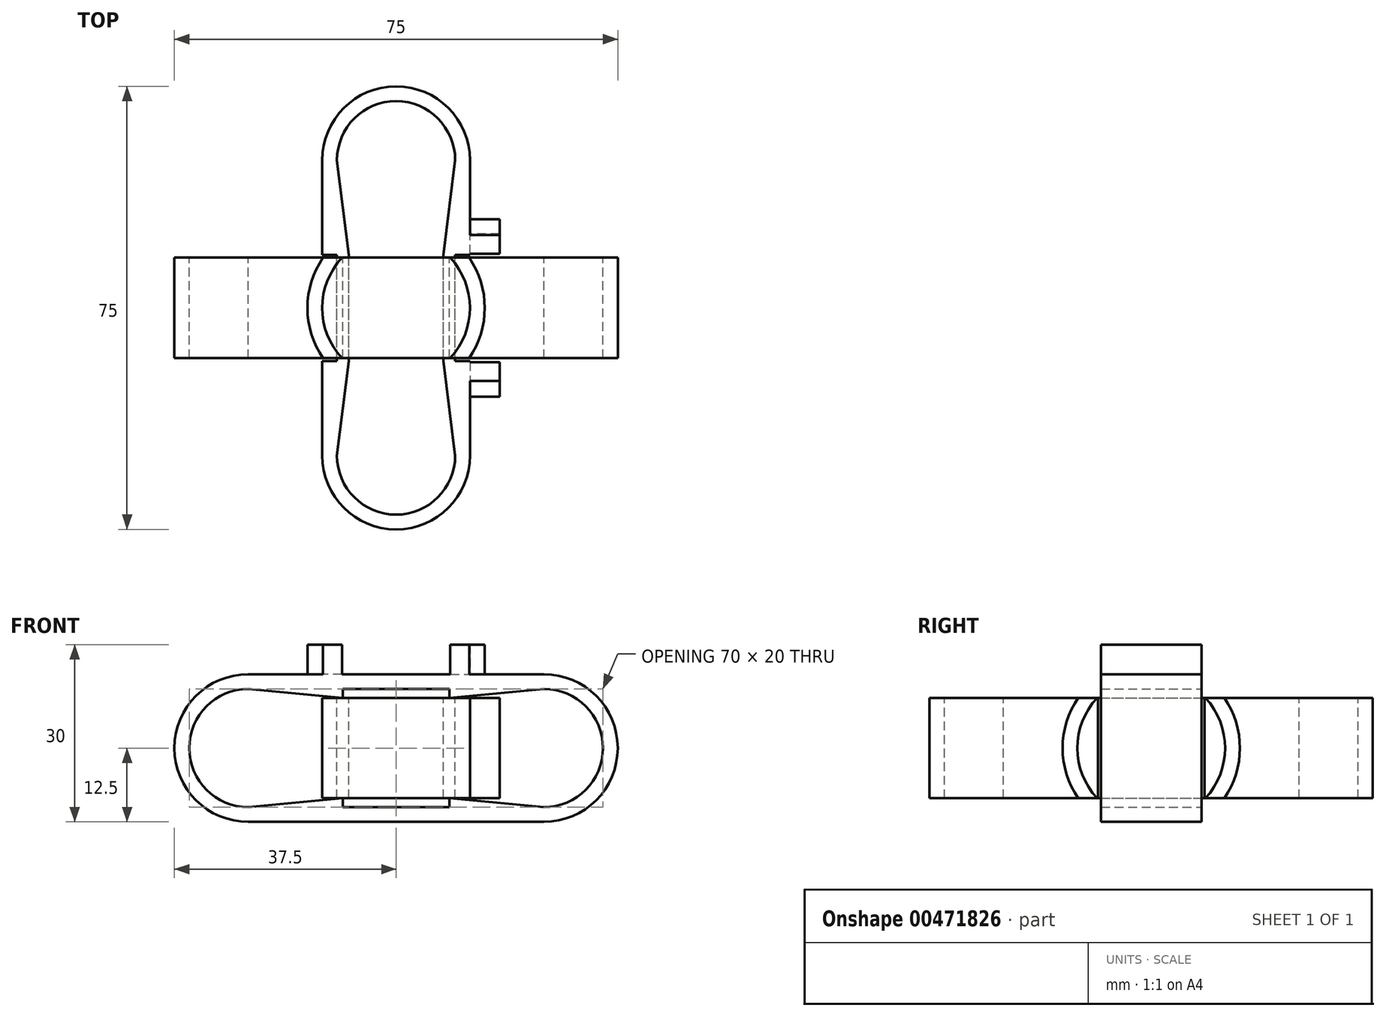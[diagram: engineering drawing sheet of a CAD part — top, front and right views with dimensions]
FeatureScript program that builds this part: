
annotation { "Feature Type Name" : "Feature", "Feature Type Description" : "" }
export const myFeature = defineFeature(function(context is Context, id is Id, definition is map)
    precondition{}
    {
        {
            var Q0;
            Q0=qCreatedBy(makeId("Front.planeOp"),FACE);
            var sketch = newSketch(context, id + "F0", { "sketchPlane" : qUnion([Q0])});
            skArc(sketch, "E0", {"start": v(-25, 12.5) * mm, "mid": v(-37.5, 0) * mm, "end": v(-25, -12.5) * mm});
            skArc(sketch, "E1", {"start": v(25, -12.5) * mm, "mid": v(37.5, 0) * mm, "end": v(25, 12.5) * mm});
            skLineSegment(sketch, "E2", {"start": v(-25, 12.5) * mm, "end": v(25, 12.5) * mm});
            skLineSegment(sketch, "E3", {"start": v(-25, -12.5) * mm, "end": v(25, -12.5) * mm});
            skPoint(sketch, "E4", {"position": v(0, 12.5) * mm});
            skArc(sketch, "E5.0", {"start": v(-25, 10) * mm, "mid": v(-35, 0) * mm, "end": v(-25, -10) * mm});
            skLineSegment(sketch, "E5.1", {"start": v(-9, 10) * mm, "end": v(9, 10) * mm});
            skArc(sketch, "E5.2", {"start": v(25, -10) * mm, "mid": v(35, 0) * mm, "end": v(25, 10) * mm});
            skLineSegment(sketch, "E5.3", {"start": v(-9, -10) * mm, "end": v(9, -10) * mm});
            skLineSegment(sketch, "E6", {"start": v(-9, 10) * mm, "end": v(-9, 8.5) * mm});
            skLineSegment(sketch, "E7", {"start": v(9, 8.5) * mm, "end": v(9, 10) * mm});
            skLineSegment(sketch, "E8", {"start": v(-25, 10) * mm, "end": v(-9, 8.5) * mm});
            skLineSegment(sketch, "E9", {"start": v(9, 8.5) * mm, "end": v(25, 10) * mm});
            skLineSegment(sketch, "E10", {"start": v(-25, 0) * mm, "end": v(25, 0) * mm, "construction": true});
            skPoint(sketch, "E11", {"position": v(0, 10) * mm});
            skLineSegment(sketch, "E12.MirrorCS", {"start": v(-25, -10) * mm, "end": v(-9, -8.5) * mm});
            skLineSegment(sketch, "E13.MirrorCS", {"start": v(-9, -10) * mm, "end": v(-9, -8.5) * mm});
            skLineSegment(sketch, "E14.MirrorCS", {"start": v(9, -8.5) * mm, "end": v(9, -10) * mm});
            skLineSegment(sketch, "E15.MirrorCS", {"start": v(9, -8.5) * mm, "end": v(25, -10) * mm});
            skSolve(sketch);
        }
        {
            var Q0;
            Q0=makeQuery(id+"F0.imprint","IMPRINT",FACE,{"disambiguationData":[TD([[makeQuery(id+"F0.imprint","IMPRINT",EDGE,{"derivedFrom":sQuery(id+"F0.wireOp",EDGE,"E0")}),1.0]])]});
            extrude(context, id + "F1", {"entities" : qUnion([Q0]), "depth" : 8.5 * mm, "hasSecondDirection" : true, "secondDirectionOppositeDirection" : true, "secondDirectionDepth" : 8.5 * mm});
        }
        {
            var Q0;
            Q0=qCreatedBy(makeId("Right.planeOp"),FACE);
            var sketch = newSketch(context, id + "F2", { "sketchPlane" : qUnion([Q0])});
            skArc(sketch, "E16", {"start": v(-25, 12.5) * mm, "mid": v(-37.5, 0) * mm, "end": v(-25, -12.5) * mm});
            skArc(sketch, "E17", {"start": v(25, -12.5) * mm, "mid": v(37.5, 0) * mm, "end": v(25, 12.5) * mm});
            skLineSegment(sketch, "E18", {"start": v(-25, 12.5) * mm, "end": v(-9, 12.5) * mm});
            skArc(sketch, "E19.0", {"start": v(-25, 10) * mm, "mid": v(-35, 0) * mm, "end": v(-25, -10) * mm});
            skLineSegment(sketch, "E19.1", {"start": v(-9, 10) * mm, "end": v(9, 10) * mm});
            skArc(sketch, "E19.2", {"start": v(25, -10) * mm, "mid": v(35, 0) * mm, "end": v(25, 10) * mm});
            skLineSegment(sketch, "E20", {"start": v(-25, 10) * mm, "end": v(-9, 8) * mm});
            skLineSegment(sketch, "E21", {"start": v(9, 8) * mm, "end": v(25, 10) * mm});
            skLineSegment(sketch, "E22", {"start": v(-25, 0) * mm, "end": v(25, 0) * mm, "construction": true});
            skPoint(sketch, "E23", {"position": v(0, 10) * mm});
            skLineSegment(sketch, "E24", {"start": v(-9, 12.5) * mm, "end": v(-9, 10) * mm});
            skLineSegment(sketch, "E25", {"start": v(9, 12.5) * mm, "end": v(9, 10) * mm});
            skLineSegment(sketch, "E26.trimOffspring", {"start": v(9, 12.5) * mm, "end": v(25, 12.5) * mm});
            skLineSegment(sketch, "E27", {"start": v(-9, 8) * mm, "end": v(9, 8) * mm});
            skPoint(sketch, "E28", {"position": v(0, 8) * mm});
            skLineSegment(sketch, "E29.MirrorCS", {"start": v(-25, -10) * mm, "end": v(-9, -8) * mm});
            skLineSegment(sketch, "E30.MirrorCS", {"start": v(-25, -12.5) * mm, "end": v(-9, -12.5) * mm});
            skLineSegment(sketch, "E31.MirrorCS", {"start": v(-9, -12.5) * mm, "end": v(-9, -10) * mm});
            skLineSegment(sketch, "E32.MirrorCS", {"start": v(-9, -10) * mm, "end": v(9, -10) * mm});
            skLineSegment(sketch, "E33.MirrorCS", {"start": v(-9, -8) * mm, "end": v(9, -8) * mm});
            skLineSegment(sketch, "E34.MirrorCS", {"start": v(9, -8) * mm, "end": v(25, -10) * mm});
            skLineSegment(sketch, "E35.MirrorCS", {"start": v(9, -12.5) * mm, "end": v(9, -10) * mm});
            skLineSegment(sketch, "E36.MirrorCS", {"start": v(9, -12.5) * mm, "end": v(25, -12.5) * mm});
            skSolve(sketch);
        }
        {
            var Q0;
            Q0=makeQuery(id+"F2.imprint","IMPRINT",FACE,{"disambiguationData":[TD([[makeQuery(id+"F2.imprint","IMPRINT",EDGE,{"derivedFrom":sQuery(id+"F2.wireOp",EDGE,"E16")}),1.0]])]});
            extrude(context, id + "F3", {"entities" : qUnion([Q0]), "depth" : 8.5 * mm, "hasSecondDirection" : true, "secondDirectionOppositeDirection" : true, "secondDirectionDepth" : 8.5 * mm});
        }
        {
            var Q0;
            Q0=makeQuery(id+"F1.opExtrude","SWEPT_FACE",FACE,{"disambiguationData":[OSD([sQuery(id+"F0.wireOp",EDGE,"E2")])]});
            var sketch = newSketch(context, id + "F4", { "sketchPlane" : qUnion([Q0])});
            skCircle(sketch, "E37", {"center": v(0, 0) * mm, "radius": 12.5 * mm});
            skCircle(sketch, "E38.0", {"center": v(0, 0) * mm, "radius": 15 * mm});
            skLineSegment(sketch, "E39", {"start": v(-8.67, 9) * mm, "end": v(-10.4, 10.8) * mm});
            skLineSegment(sketch, "E40", {"start": v(8.67, 9) * mm, "end": v(10.4, 10.8) * mm});
            skLineSegment(sketch, "E41", {"start": v(-8.67, 9) * mm, "end": v(0, 0) * mm, "construction": true});
            skLineSegment(sketch, "E42", {"start": v(0, 0) * mm, "end": v(8.67, 9) * mm, "construction": true});
            skLineSegment(sketch, "E43", {"start": v(0, 0) * mm, "end": v(-12.36, 8.5) * mm});
            skLineSegment(sketch, "E44", {"start": v(0, 0) * mm, "end": v(12.36, 8.5) * mm});
            skLineSegment(sketch, "E45", {"start": v(-12.5, 0) * mm, "end": v(12.5, 0) * mm, "construction": true});
            skLineSegment(sketch, "E46.MirrorCS", {"start": v(0, 0) * mm, "end": v(-12.36, -8.5) * mm});
            skLineSegment(sketch, "E47.MirrorCS", {"start": v(-8.67, -9) * mm, "end": v(-10.4, -10.8) * mm});
            skLineSegment(sketch, "E48.MirrorCS", {"start": v(8.67, -9) * mm, "end": v(10.4, -10.8) * mm});
            skLineSegment(sketch, "E49.MirrorCS", {"start": v(0, 0) * mm, "end": v(12.36, -8.5) * mm});
            skLineSegment(sketch, "E50.0", {"start": v(-8.5, 9) * mm, "end": v(-8.5, 25) * mm});
            skLineSegment(sketch, "E51.0", {"start": v(8.5, 9) * mm, "end": v(-8.5, 9) * mm});
            skLineSegment(sketch, "E52.0", {"start": v(8.5, 9) * mm, "end": v(8.5, 25) * mm});
            skLineSegment(sketch, "E53.0", {"start": v(8.5, -9) * mm, "end": v(-8.5, -9) * mm});
            skLineSegment(sketch, "E54.0", {"start": v(8.5, -25) * mm, "end": v(8.5, -9) * mm});
            skLineSegment(sketch, "E55.0", {"start": v(-8.5, -25) * mm, "end": v(-8.5, -9) * mm});
            skSolve(sketch);
        }
        {
            var Q0;
            {var subQ0=sQuery(id+"F4.wireOp",EDGE,"E43");var subQ1=sQuery(id+"F4.wireOp",EDGE,"E37");var subQ2=makeQuery(id+"F4.imprint","INTERSECT",VERTEX,{"derivedFrom":[subQ1,subQ0]});Q0=makeQuery(id+"F4.imprint","IMPRINT",FACE,{"disambiguationData":[TD([[makeQuery(id+"F4.imprint","IMPRINT",EDGE,{"disambiguationData":[TD([[subQ2,-1.0]])],"derivedFrom":subQ1}),-1.0]])]});}
            var Q1;
            {var subQ0=sQuery(id+"F4.wireOp",EDGE,"E44");var subQ1=sQuery(id+"F4.wireOp",EDGE,"E37");var subQ2=makeQuery(id+"F4.imprint","INTERSECT",VERTEX,{"derivedFrom":[subQ1,subQ0]});Q1=makeQuery(id+"F4.imprint","IMPRINT",FACE,{"disambiguationData":[TD([[makeQuery(id+"F4.imprint","IMPRINT",EDGE,{"disambiguationData":[TD([[subQ2,1.0]])],"derivedFrom":subQ1}),-1.0]])]});}
            var Q2;
            {var subQ0=sQuery(id+"F4.wireOp",EDGE,"E43");var subQ1=sQuery(id+"F4.wireOp",EDGE,"E37");var subQ2=makeQuery(id+"F4.imprint","INTERSECT",VERTEX,{"derivedFrom":[subQ1,subQ0]});Q2=makeQuery(id+"F4.imprint","IMPRINT",FACE,{"disambiguationData":[TD([[makeQuery(id+"F4.imprint","IMPRINT",EDGE,{"disambiguationData":[TD([[subQ2,1.0]])],"derivedFrom":subQ1}),-1.0]])]});}
            var Q3;
            {var subQ0=sQuery(id+"F4.wireOp",EDGE,"E44");var subQ1=sQuery(id+"F4.wireOp",EDGE,"E37");var subQ2=makeQuery(id+"F4.imprint","INTERSECT",VERTEX,{"derivedFrom":[subQ1,subQ0]});Q3=makeQuery(id+"F4.imprint","IMPRINT",FACE,{"disambiguationData":[TD([[makeQuery(id+"F4.imprint","IMPRINT",EDGE,{"disambiguationData":[TD([[subQ2,-1.0]])],"derivedFrom":subQ1}),-1.0]])]});}
            var Q4;
            {var subQ0=sQuery(id+"F4.wireOp",EDGE,"E49.MirrorCS");var subQ1=sQuery(id+"F4.wireOp",EDGE,"E37");var subQ2=makeQuery(id+"F4.imprint","INTERSECT",VERTEX,{"derivedFrom":[subQ1,subQ0]});Q4=makeQuery(id+"F4.imprint","IMPRINT",FACE,{"disambiguationData":[TD([[makeQuery(id+"F4.imprint","IMPRINT",EDGE,{"disambiguationData":[TD([[subQ2,1.0]])],"derivedFrom":subQ1}),-1.0]])]});}
            var Q5;
            {var subQ0=sQuery(id+"F4.wireOp",EDGE,"E46.MirrorCS");var subQ1=sQuery(id+"F4.wireOp",EDGE,"E37");var subQ2=makeQuery(id+"F4.imprint","INTERSECT",VERTEX,{"derivedFrom":[subQ1,subQ0]});Q5=makeQuery(id+"F4.imprint","IMPRINT",FACE,{"disambiguationData":[TD([[makeQuery(id+"F4.imprint","IMPRINT",EDGE,{"disambiguationData":[TD([[subQ2,-1.0]])],"derivedFrom":subQ1}),-1.0]])]});}
            extrude(context, id + "F5", {"entities" : qUnion([Q0, Q1, Q2, Q3, Q4, Q5]), "operationType" : NewBodyOperationType.ADD, "depth" : 5 * mm});
        }
        {
            var Q0;
            {var subQ0=sQuery(id+"F4.wireOp",EDGE,"E52.0");var subQ1=sQuery(id+"F4.wireOp",EDGE,"E37");var subQ2=makeQuery(id+"F4.imprint","INTERSECT",VERTEX,{"derivedFrom":[subQ1,subQ0]});Q0=makeQuery(id+"F4.imprint","IMPRINT",FACE,{"disambiguationData":[TD([[makeQuery(id+"F4.imprint","IMPRINT",EDGE,{"disambiguationData":[TD([[subQ2,-1.0]])],"derivedFrom":subQ1}),-1.0]])]});}
            var Q1;
            {var subQ0=sQuery(id+"F4.wireOp",EDGE,"E55.0");var subQ1=sQuery(id+"F4.wireOp",EDGE,"E37");var subQ2=makeQuery(id+"F4.imprint","INTERSECT",VERTEX,{"derivedFrom":[subQ1,subQ0]});Q1=makeQuery(id+"F4.imprint","IMPRINT",FACE,{"disambiguationData":[TD([[makeQuery(id+"F4.imprint","IMPRINT",EDGE,{"disambiguationData":[TD([[subQ2,-1.0]])],"derivedFrom":subQ1}),-1.0]])]});}
            extrude(context, id + "F6", {"entities" : qUnion([Q0, Q1]), "operationType" : NewBodyOperationType.ADD, "depth" : 5 * mm});
        }
        {
            var Q0;
            Q0=makeQuery(id+"F3.opExtrude","SWEPT_BODY",BODY,{"disambiguationData":[OSD([sQuery(id+"F2.wireOp",EDGE,"E16"),sQuery(id+"F2.wireOp",EDGE,"E17"),sQuery(id+"F2.wireOp",EDGE,"E18"),sQuery(id+"F2.wireOp",EDGE,"E19.0"),sQuery(id+"F2.wireOp",EDGE,"E19.1"),sQuery(id+"F2.wireOp",EDGE,"E19.2"),sQuery(id+"F2.wireOp",EDGE,"E20"),sQuery(id+"F2.wireOp",EDGE,"E21"),sQuery(id+"F2.wireOp",EDGE,"E24"),sQuery(id+"F2.wireOp",EDGE,"E25"),sQuery(id+"F2.wireOp",EDGE,"E26.trimOffspring"),sQuery(id+"F2.wireOp",EDGE,"E27"),sQuery(id+"F2.wireOp",EDGE,"E29.MirrorCS"),sQuery(id+"F2.wireOp",EDGE,"E30.MirrorCS"),sQuery(id+"F2.wireOp",EDGE,"E31.MirrorCS"),sQuery(id+"F2.wireOp",EDGE,"E32.MirrorCS"),sQuery(id+"F2.wireOp",EDGE,"E33.MirrorCS"),sQuery(id+"F2.wireOp",EDGE,"E34.MirrorCS"),sQuery(id+"F2.wireOp",EDGE,"E35.MirrorCS"),sQuery(id+"F2.wireOp",EDGE,"E36.MirrorCS")])]});
            var Q1;
            Q1=sQuery(id+"F2.wireOp",EDGE,"E22");
            transform(context, id + "F7", {"entities" : qUnion([Q0]), "transformType" : TransformType.ROTATION, "transformAxis" : qUnion([Q1]), "angle" : 90 * degree, "makeCopy" : false});
        }
    });
